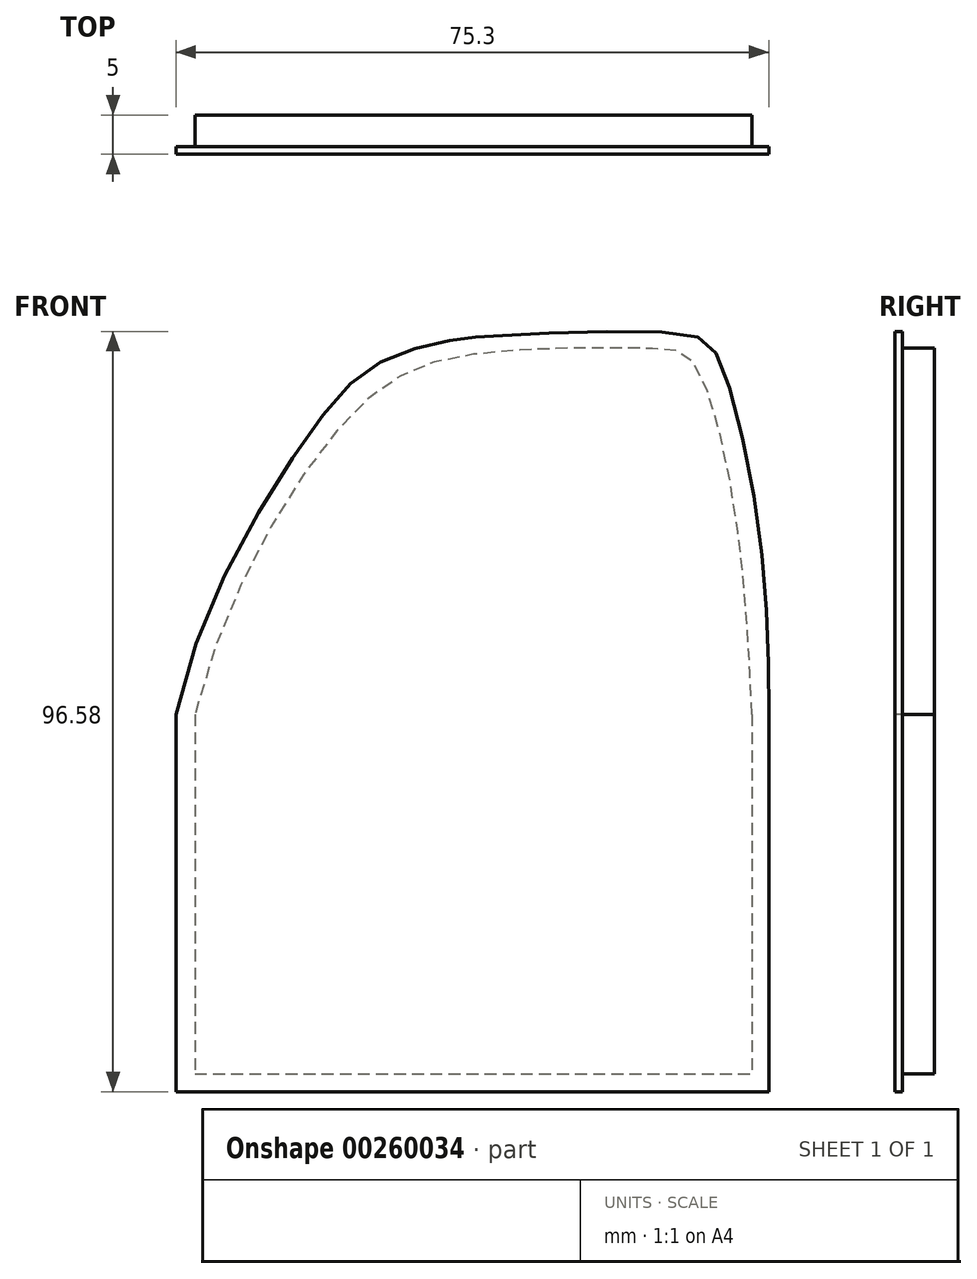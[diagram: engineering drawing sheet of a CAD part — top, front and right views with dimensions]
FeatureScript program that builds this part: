
annotation { "Feature Type Name" : "Feature", "Feature Type Description" : "" }
export const myFeature = defineFeature(function(context is Context, id is Id, definition is map)
    precondition{}
    {
        {
            var Q0;
            Q0=qCreatedBy(makeId("Front.planeOp"),FACE);
            var sketch = newSketch(context, id + "F0", { "sketchPlane" : qUnion([Q0])});
            skLineSegment(sketch, "E0.bottom", {"start": v(-6.38, 46.5) * mm, "end": v(21.95, 46.5) * mm});
            skLineSegment(sketch, "E0.top", {"start": v(-46.59, -55.14) * mm, "end": v(33.83, -55.14) * mm});
            skLineSegment(sketch, "E0.left", {"start": v(-46.59, -4.32) * mm, "end": v(-46.59, -55.14) * mm});
            skLineSegment(sketch, "E0.right", {"start": v(33.83, 19.6) * mm, "end": v(33.83, -55.14) * mm});
            skFitSpline(sketch, "E1", {"points": [v(-46.59, -4.32) * mm, v(-30.87, 31) * mm, v(-20.25, 41.13) * mm, v(-6.38, 46.5) * mm], "startDerivative": vector(17.33, 88.44) * mm, "endDerivative": vector(60.56, 8.43) * mm});
            skPoint(sketch, "E2.orphan", {"position": v(-46.59, 46.5) * mm});
            skFitSpline(sketch, "E3", {"points": [v(21.95, 46.5) * mm, v(27.63, 41.64) * mm, v(33.83, 19.6) * mm, v(33.83, 3.49) * mm, v(33.83, 3.37) * mm], "startDerivative": vector(25.35, -15.2) * mm, "endDerivative": vector(0.18, -3.1) * mm});
            skPoint(sketch, "E4.orphan", {"position": v(33.83, 46.5) * mm});
            skLineSegment(sketch, "E5.top", {"start": v(-43.68, -52.26) * mm, "end": v(31.62, -52.26) * mm});
            skLineSegment(sketch, "E5.left", {"start": v(-43.68, -4.32) * mm, "end": v(-43.68, -52.26) * mm});
            skLineSegment(sketch, "E5.right", {"start": v(31.62, -4.32) * mm, "end": v(31.62, -52.26) * mm});
            skFitSpline(sketch, "E6", {"points": [v(-43.68, -4.32) * mm, v(-27, 31) * mm, v(-17.27, 40.65) * mm, v(-7.5, 43.38) * mm, v(-1.6, 43.84) * mm, v(20.74, 44) * mm, v(25.12, 41.13) * mm, v(30.28, 19.6) * mm, v(31.62, -4.32) * mm], "startDerivative": vector(40.76, 206.76) * mm, "endDerivative": vector(0.55, -146.46) * mm});
            skLineSegment(sketch, "E7.top", {"start": v(-41.28, -50.03) * mm, "end": v(29.47, -50.03) * mm});
            skLineSegment(sketch, "E7.left", {"start": v(-41.28, -4.32) * mm, "end": v(-41.28, -50.03) * mm});
            skLineSegment(sketch, "E7.right", {"start": v(29.47, -4.32) * mm, "end": v(29.47, -50.03) * mm});
            skFitSpline(sketch, "E8", {"points": [v(29.47, -4.32) * mm, v(27.6, 19.6) * mm, v(21.96, 40.45) * mm, v(16.9, 42.14) * mm, v(-5.95, 41.4) * mm, v(-20.95, 34.2) * mm, v(-41.28, -4.32) * mm], "startDerivative": vector(-5.83, 122.07) * mm, "endDerivative": vector(-47.07, -192.85) * mm});
            skSolve(sketch);
        }
        {
            var Q0;
            Q0=makeQuery(id+"F0.imprint","IMPRINT",FACE,{"disambiguationData":[TD([[makeQuery(id+"F0.imprint","IMPRINT",EDGE,{"derivedFrom":sQuery(id+"F0.wireOp",EDGE,"E5.top")}),1.0]])]});
            extrude(context, id + "F1", {"entities" : qUnion([Q0]), "oppositeDirection" : true, "depth" : 1 * mm});
        }
        {
            var Q0;
            Q0=makeQuery(id+"F0.imprint","IMPRINT",FACE,{"disambiguationData":[TD([[makeQuery(id+"F0.imprint","IMPRINT",EDGE,{"derivedFrom":sQuery(id+"F0.wireOp",EDGE,"E7.top")}),1.0]])]});
            extrude(context, id + "F2", {"entities" : qUnion([Q0]), "operationType" : NewBodyOperationType.ADD, "oppositeDirection" : true, "depth" : 5 * mm});
        }
    });
